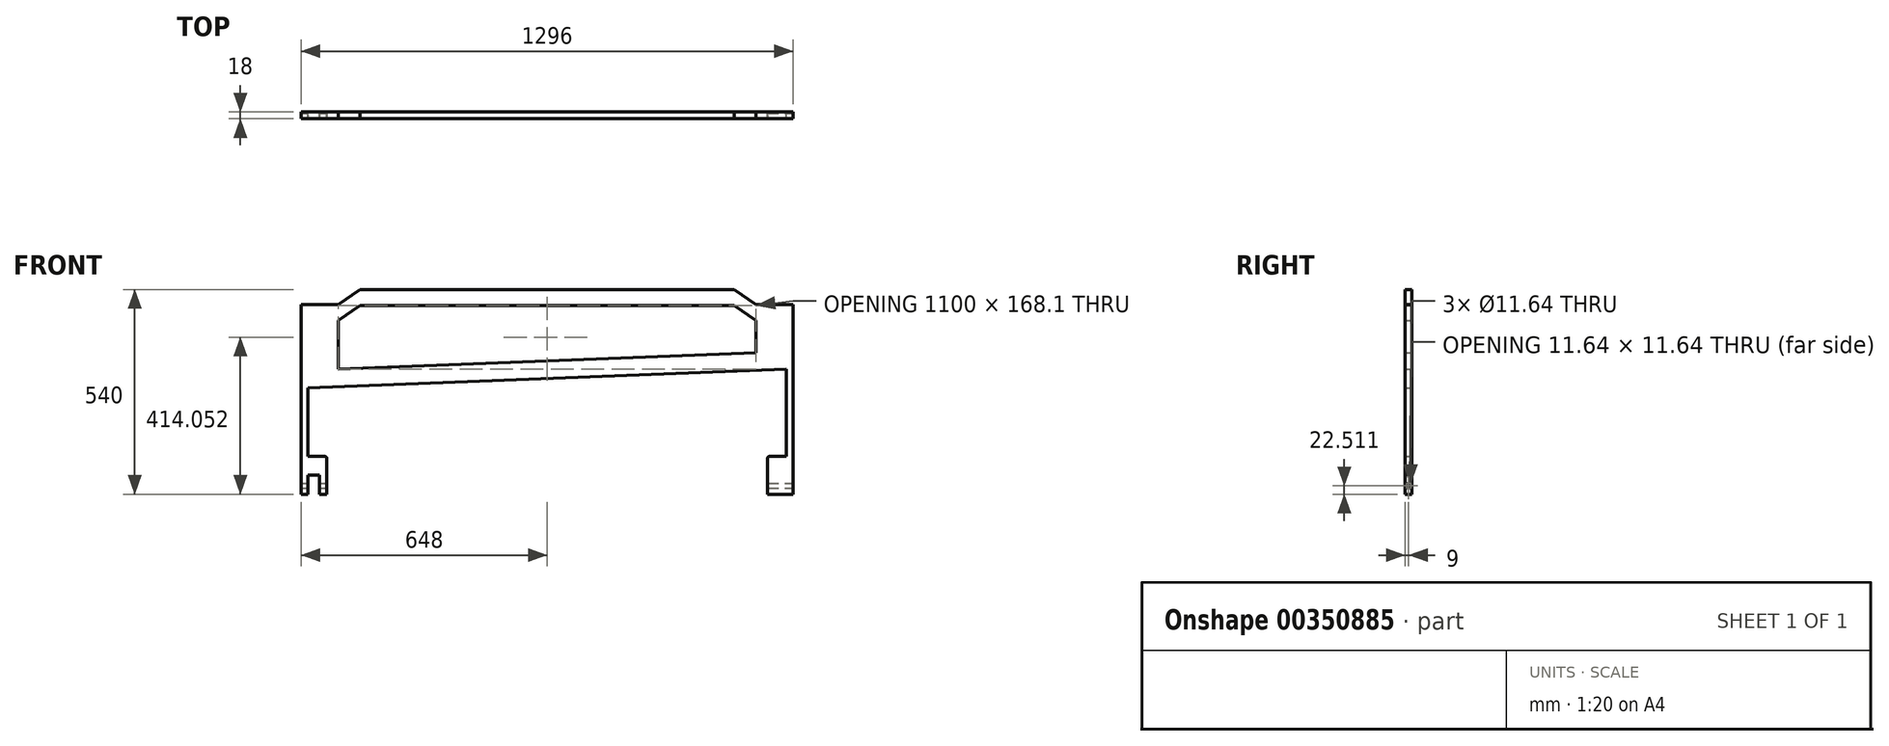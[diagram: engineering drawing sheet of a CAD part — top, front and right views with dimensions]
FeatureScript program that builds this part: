
annotation { "Feature Type Name" : "Feature", "Feature Type Description" : "" }
export const myFeature = defineFeature(function(context is Context, id is Id, definition is map)
    precondition{}
    {
        {
            var Q0;
            Q0=qCreatedBy(makeId("Front.planeOp"),FACE);
            var sketch = newSketch(context, id + "F0", { "sketchPlane" : qUnion([Q0])});
            skLineSegment(sketch, "E0", {"start": v(0, 210) * mm, "end": v(492.55, 210) * mm});
            skLineSegment(sketch, "E1", {"start": v(492.55, 210) * mm, "end": v(550, 170) * mm});
            skLineSegment(sketch, "E2", {"start": v(550, 170) * mm, "end": v(630, 170) * mm});
            skLineSegment(sketch, "E3.MirrorCS", {"start": v(-492.55, 210) * mm, "end": v(-550, 170) * mm});
            skLineSegment(sketch, "E4.MirrorCS", {"start": v(-550, 170) * mm, "end": v(-630, 170) * mm});
            skLineSegment(sketch, "E5.MirrorCS", {"start": v(0, 210) * mm, "end": v(-492.55, 210) * mm});
            skLineSegment(sketch, "E6", {"start": v(-630, -50) * mm, "end": v(630, 0) * mm});
            skLineSegment(sketch, "E7", {"start": v(-630, 170) * mm, "end": v(-648, 170) * mm});
            skLineSegment(sketch, "E8", {"start": v(-648, 170) * mm, "end": v(-648, -330) * mm});
            skLineSegment(sketch, "E9", {"start": v(-648, -330) * mm, "end": v(-630, -330) * mm});
            skLineSegment(sketch, "E10", {"start": v(-630, -330) * mm, "end": v(-630, -280) * mm});
            skLineSegment(sketch, "E11.MirrorCS", {"start": v(630, 170) * mm, "end": v(648, 170) * mm});
            skLineSegment(sketch, "E12.MirrorCS", {"start": v(648, -330) * mm, "end": v(630, -330) * mm});
            skLineSegment(sketch, "E13.MirrorCS", {"start": v(648, 170) * mm, "end": v(648, -330) * mm});
            skLineSegment(sketch, "E14.MirrorCS", {"start": v(630, -330) * mm, "end": v(630, -280) * mm});
            skLineSegment(sketch, "E15.MirrorCS", {"start": v(630, 0) * mm, "end": v(630, -50) * mm});
            skLineSegment(sketch, "E16.bottom", {"start": v(-648, -330) * mm, "end": v(-580, -330) * mm});
            skLineSegment(sketch, "E16.top", {"start": v(-630, -230) * mm, "end": v(-586.35, -230) * mm});
            skLineSegment(sketch, "E16.left", {"start": v(-648, -330) * mm, "end": v(-648, -230) * mm});
            skLineSegment(sketch, "E16.right", {"start": v(-580, -330) * mm, "end": v(-580, -236.35) * mm});
            skLineSegment(sketch, "E17.bottom", {"start": v(-630, -330) * mm, "end": v(-600, -330) * mm});
            skLineSegment(sketch, "E17.top", {"start": v(-630, -280) * mm, "end": v(-600, -280) * mm});
            skLineSegment(sketch, "E17.right", {"start": v(-600, -330) * mm, "end": v(-600, -280) * mm});
            skLineSegment(sketch, "E18.trimOffspring", {"start": v(-630, -230) * mm, "end": v(-630, -50) * mm});
            skLineSegment(sketch, "E19.MirrorCS", {"start": v(630, -330) * mm, "end": v(600, -330) * mm});
            skLineSegment(sketch, "E20.MirrorCS", {"start": v(648, -330) * mm, "end": v(648, -230) * mm});
            skLineSegment(sketch, "E21.MirrorCS", {"start": v(630, -230) * mm, "end": v(630, -50) * mm});
            skLineSegment(sketch, "E22.MirrorCS", {"start": v(580, -330) * mm, "end": v(580, -236.35) * mm});
            skLineSegment(sketch, "E23.MirrorCS", {"start": v(648, -330) * mm, "end": v(580, -330) * mm});
            skLineSegment(sketch, "E24.MirrorCS", {"start": v(630, -280) * mm, "end": v(600, -280) * mm});
            skLineSegment(sketch, "E25.MirrorCS", {"start": v(630, -230) * mm, "end": v(586.35, -230) * mm});
            skLineSegment(sketch, "E26.MirrorCS", {"start": v(600, -330) * mm, "end": v(600, -280) * mm});
            skPoint(sketch, "E27.visualSharp", {"position": v(-580, -230) * mm});
            skArc(sketch, "E27.filletArc", {"start": v(-580, -236.35) * mm, "mid": v(-581.86, -231.86) * mm, "end": v(-586.35, -230) * mm});
            skPoint(sketch, "E28.visualSharp", {"position": v(580, -230) * mm});
            skArc(sketch, "E28.filletArc", {"start": v(586.35, -230) * mm, "mid": v(581.86, -231.86) * mm, "end": v(580, -236.35) * mm});
            skLineSegment(sketch, "E29", {"start": v(-550, 0) * mm, "end": v(-550, 128.1) * mm});
            skLineSegment(sketch, "E30", {"start": v(-550, 128.1) * mm, "end": v(-492.55, 168.1) * mm});
            skLineSegment(sketch, "E31", {"start": v(-492.55, 168.1) * mm, "end": v(492.55, 168.1) * mm});
            skLineSegment(sketch, "E32", {"start": v(492.55, 168.1) * mm, "end": v(550, 128.1) * mm});
            skLineSegment(sketch, "E33", {"start": v(550, 128.1) * mm, "end": v(550, 43.65) * mm});
            skLineSegment(sketch, "E34", {"start": v(550, 43.65) * mm, "end": v(-550, 0) * mm});
            skPoint(sketch, "E35.orphan", {"position": v(630, 170) * mm});
            skSolve(sketch);
        }
        {
            var Q0;
            Q0=makeQuery(id+"F0.imprint","IMPRINT",FACE,{"disambiguationData":[TD([[makeQuery(id+"F0.imprint","IMPRINT",EDGE,{"derivedFrom":sQuery(id+"F0.wireOp",EDGE,"E0")}),-1.0]])]});
            var Q1;
            Q1=makeQuery(id+"F0.imprint","IMPRINT",FACE,{"disambiguationData":[TD([[makeQuery(id+"F0.imprint","IMPRINT",EDGE,{"derivedFrom":sQuery(id+"F0.wireOp",EDGE,"E14.MirrorCS")}),1.0]])]});
            var Q2;
            {var subQ3=sQuery(id+"F0.wireOp",EDGE,"E11.MirrorCS");Q2=makeQuery(id+"F0.imprint","IMPRINT",FACE,{"disambiguationData":[TD([[makeQuery(id+"F0.imprint","IMPRINT",EDGE,{"derivedFrom":subQ3}),-1.0]])]});}
            var Q3;
            Q3=makeQuery(id+"F0.imprint","IMPRINT",FACE,{"disambiguationData":[TD([[makeQuery(id+"F0.imprint","IMPRINT",EDGE,{"derivedFrom":sQuery(id+"F0.wireOp",EDGE,"usrydNuo-TQOn-QbON-Jcbg-NNstnUplL0ps")}),-1.0]])]});
            extrude(context, id + "F1", {"entities" : qUnion([Q0, Q1, Q2, Q3]), "endBound" : BoundingType.SYMMETRIC, "depth" : 18 * mm});
        }
        {
            var Q0;
            Q0=makeQuery(id+"F1.opExtrude","SWEPT_FACE",FACE,{"disambiguationData":[OSD([sQuery(id+"F0.wireOp",EDGE,"E13.MirrorCS")])]});
            var sketch = newSketch(context, id + "F2", { "sketchPlane" : qUnion([Q0])});
            skPoint(sketch, "E36.endSnap0", {"position": v(0, -330) * mm});
            skCircle(sketch, "E37", {"center": v(0, -307.49) * mm, "radius": 5.82 * mm});
            skSolve(sketch);
        }
        {
            var Q0;
            Q0=makeQuery(id+"F2.imprint","IMPRINT",FACE,{"disambiguationData":[TD([[makeQuery(id+"F2.imprint","IMPRINT",EDGE,{"derivedFrom":sQuery(id+"F2.wireOp",EDGE,"E37")}),1.0]])]});
            var Q1;
            Q1=sQuery(id+"F2.wireOp",EDGE,"E37");
            extrude(context, id + "F3", {"entities" : qUnion([Q0]), "operationType" : NewBodyOperationType.REMOVE, "surfaceEntities" : qUnion([Q1]), "oppositeDirection" : true, "depth" : 1800 * mm});
        }
    });
